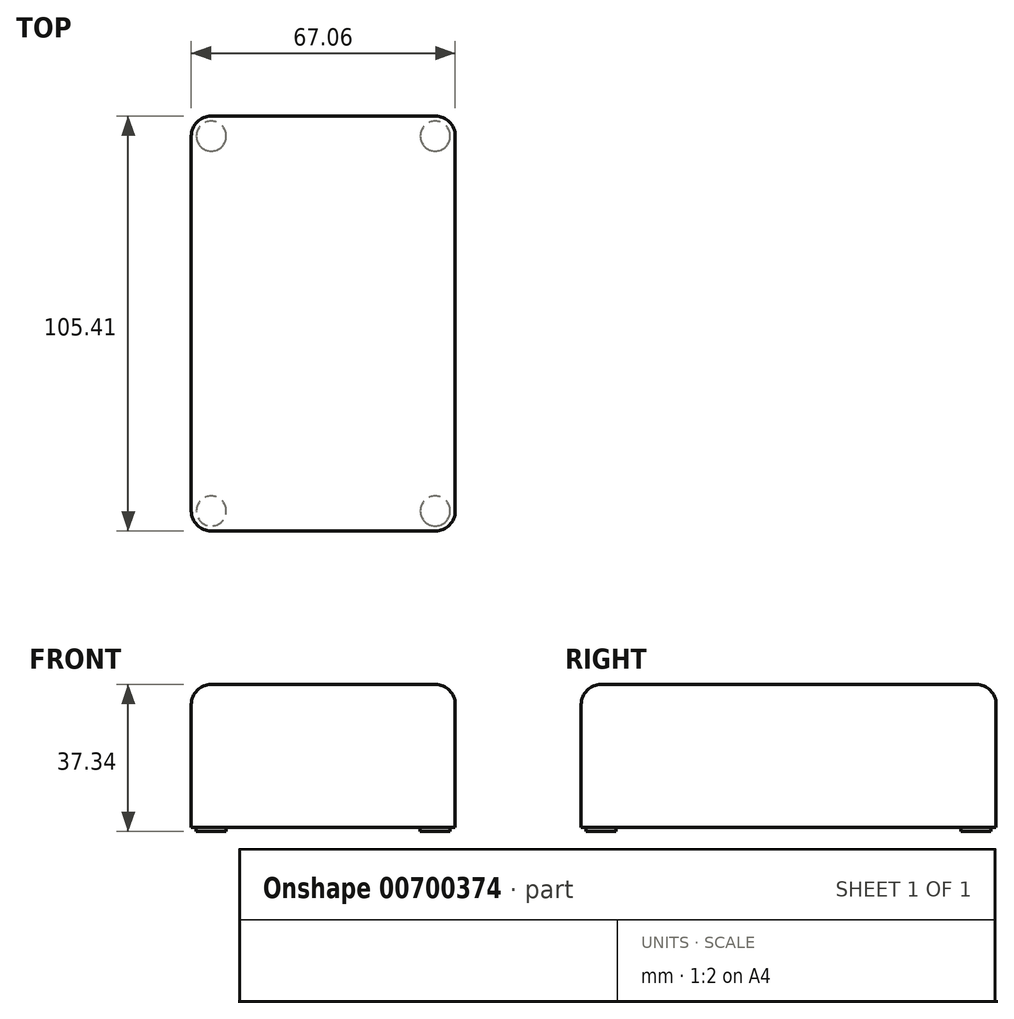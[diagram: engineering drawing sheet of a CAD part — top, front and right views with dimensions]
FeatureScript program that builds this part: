
annotation { "Feature Type Name" : "Feature", "Feature Type Description" : "" }
export const myFeature = defineFeature(function(context is Context, id is Id, definition is map)
    precondition{}
    {
        {
            var Q0;
            Q0=qCreatedBy(makeId("Top.planeOp"),FACE);
            var sketch = newSketch(context, id + "F0", { "sketchPlane" : qUnion([Q0])});
            skLineSegment(sketch, "E0.bottom", {"start": v(0, 0) * mm, "end": v(67.06, 0) * mm});
            skLineSegment(sketch, "E0.top", {"start": v(0, 105.41) * mm, "end": v(67.06, 105.41) * mm});
            skLineSegment(sketch, "E0.left", {"start": v(0, 0) * mm, "end": v(0, 105.41) * mm});
            skLineSegment(sketch, "E0.right", {"start": v(67.06, 0) * mm, "end": v(67.06, 105.4) * mm});
            skSolve(sketch);
        }
        {
            var Q0;
            Q0 = qSketchRegion(id + "F0", true);
            extrude(context, id + "F1", {"entities" : qUnion([Q0]), "depth" : 36.32 * mm, "offsetDistance" : 25.4 * mm});
        }
        {
            var Q0;
            Q0=makeQuery(id+"F1.opExtrude","SWEPT_EDGE",EDGE,{"disambiguationData":[OSD([sQuery(id+"F0.wireOp",EDGE,"E0.bottom"),sQuery(id+"F0.wireOp",EDGE,"E0.left")])]});
            var Q1;
            Q1=makeQuery(id+"F1.opExtrude","SWEPT_EDGE",EDGE,{"disambiguationData":[OSD([sQuery(id+"F0.wireOp",EDGE,"E0.bottom"),sQuery(id+"F0.wireOp",EDGE,"E0.right")])]});
            var Q2;
            Q2=makeQuery(id+"F1.opExtrude","SWEPT_EDGE",EDGE,{"disambiguationData":[OSD([sQuery(id+"F0.wireOp",EDGE,"E0.top"),sQuery(id+"F0.wireOp",EDGE,"E0.right")])]});
            var Q3;
            Q3=makeQuery(id+"F1.opExtrude","CAP_FACE",FACE,{"disambiguationData":[OSD([sQuery(id+"F0.wireOp",EDGE,"E0.bottom"),sQuery(id+"F0.wireOp",EDGE,"E0.top"),sQuery(id+"F0.wireOp",EDGE,"E0.left"),sQuery(id+"F0.wireOp",EDGE,"E0.right")])],"isStart":false});
            var Q4;
            Q4=makeQuery(id+"F1.opExtrude","SWEPT_EDGE",EDGE,{"disambiguationData":[OSD([sQuery(id+"F0.wireOp",EDGE,"E0.top"),sQuery(id+"F0.wireOp",EDGE,"E0.left")])]});
            fillet(context, id + "F2", {"entities" : qUnion([Q0, Q1, Q2, Q3, Q4]), "radius" : 5.08 * mm, "tangentPropagation" : true, "allowEdgeOverflow" : false});
        }
        {
            var Q0;
            Q0=makeQuery(id+"F1.opExtrude","CAP_FACE",FACE,{"disambiguationData":[OSD([sQuery(id+"F0.wireOp",EDGE,"E0.bottom"),sQuery(id+"F0.wireOp",EDGE,"E0.top"),sQuery(id+"F0.wireOp",EDGE,"E0.left"),sQuery(id+"F0.wireOp",EDGE,"E0.right")])],"isStart":true});
            var sketch = newSketch(context, id + "F3", { "sketchPlane" : qUnion([Q0])});
            skCircle(sketch, "E1", {"center": v(5.08, -5.08) * mm, "radius": 3.81 * mm});
            skCircle(sketch, "E2", {"center": v(61.98, -5.08) * mm, "radius": 3.81 * mm});
            skCircle(sketch, "E3", {"center": v(5.08, -100.33) * mm, "radius": 3.81 * mm});
            skCircle(sketch, "E4", {"center": v(61.98, -100.33) * mm, "radius": 3.81 * mm});
            skSolve(sketch);
        }
        {
            var Q0;
            Q0 = qSketchRegion(id + "F3", true);
            extrude(context, id + "F4", {"entities" : qUnion([Q0]), "operationType" : NewBodyOperationType.ADD, "depth" : 1.02 * mm, "offsetDistance" : 25.4 * mm});
        }
    });
